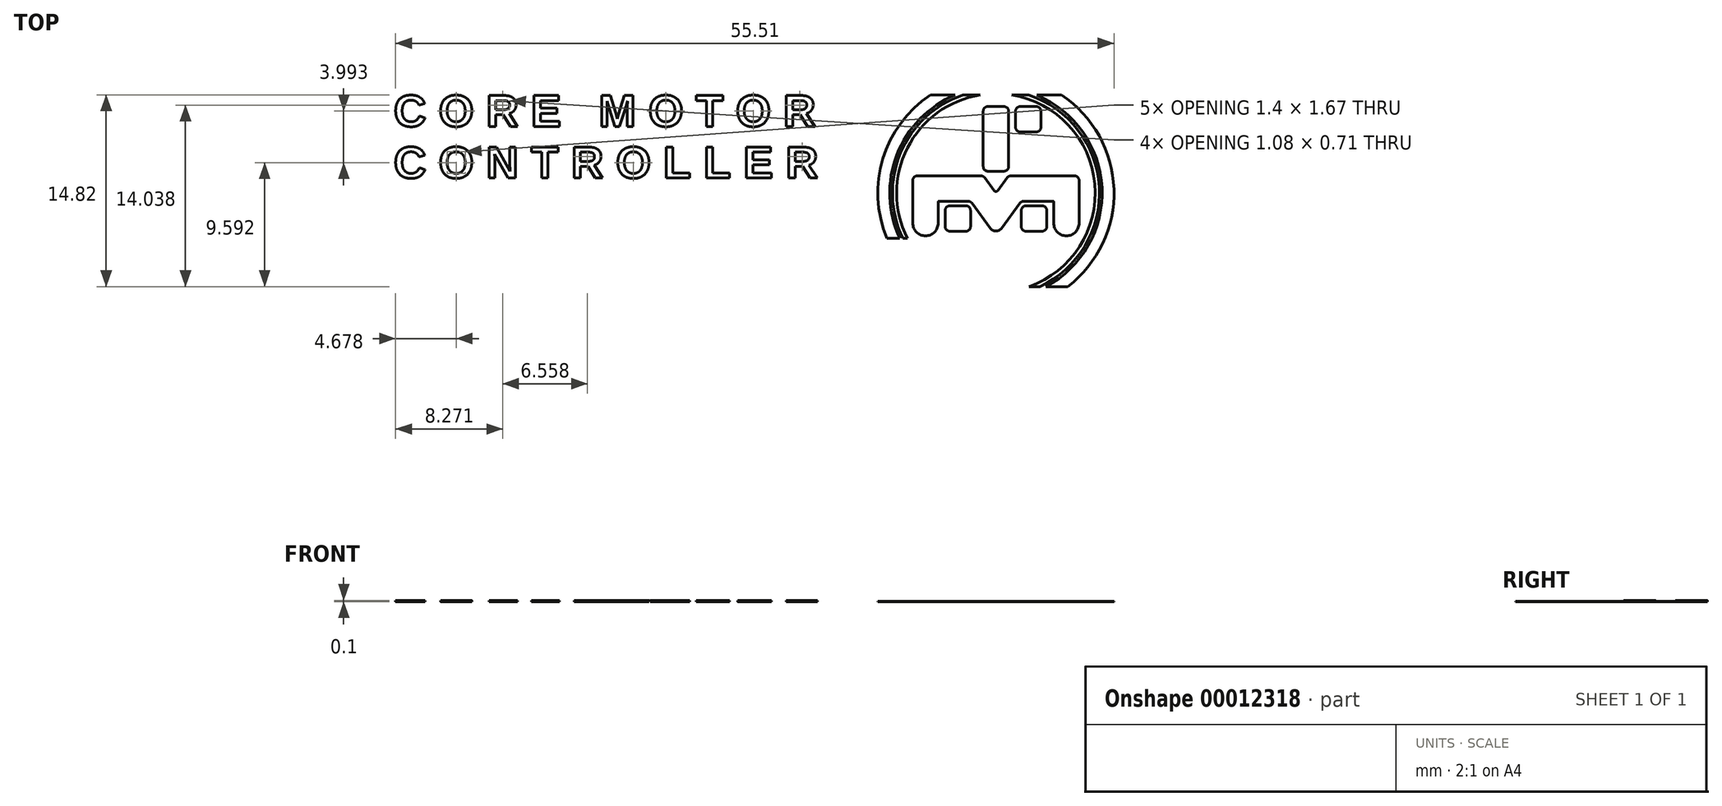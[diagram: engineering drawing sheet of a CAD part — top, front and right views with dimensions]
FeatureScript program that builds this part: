
annotation { "Feature Type Name" : "Feature", "Feature Type Description" : "" }
export const myFeature = defineFeature(function(context is Context, id is Id, definition is map)
    precondition{}
    {
        {
            var Q0;
            Q0=qCreatedBy(makeId("Top.planeOp"),FACE);
            var sketch = newSketch(context, id + "F0", { "sketchPlane" : qUnion([Q0])});
            skLineSegment(sketch, "E0.bottom", {"start": v(62.75, -5.5) * mm, "end": v(66.25, -5.5) * mm});
            skLineSegment(sketch, "E0.top", {"start": v(62.75, -19.5) * mm, "end": v(66.25, -19.5) * mm});
            skLineSegment(sketch, "E0.left", {"start": v(61.75, -6.5) * mm, "end": v(61.75, -18.5) * mm});
            skLineSegment(sketch, "E0.right", {"start": v(67.25, -6.5) * mm, "end": v(67.25, -18.5) * mm});
            skLineSegment(sketch, "E1.bottom", {"start": v(69.75, -5.5) * mm, "end": v(73.25, -5.5) * mm});
            skLineSegment(sketch, "E1.top", {"start": v(69.75, -11) * mm, "end": v(73.25, -11) * mm});
            skLineSegment(sketch, "E1.left", {"start": v(68.75, -6.5) * mm, "end": v(68.75, -10) * mm});
            skLineSegment(sketch, "E1.right", {"start": v(74.25, -6.5) * mm, "end": v(74.25, -10) * mm});
            skLineSegment(sketch, "E2", {"start": v(64.5, -19.5) * mm, "end": v(64.5, -33.5) * mm, "construction": true});
            skLineSegment(sketch, "E3", {"start": v(63.3, -31.86) * mm, "end": v(59.27, -26.4) * mm});
            skLineSegment(sketch, "E4", {"start": v(58.47, -26) * mm, "end": v(52.1, -26) * mm});
            skLineSegment(sketch, "E5", {"start": v(52, -26.1) * mm, "end": v(52, -30.75) * mm});
            skLineSegment(sketch, "E6.0", {"start": v(46.5, -21.5) * mm, "end": v(46.5, -30.75) * mm});
            skLineSegment(sketch, "E6.1", {"start": v(61.24, -20.5) * mm, "end": v(47.5, -20.5) * mm});
            skLineSegment(sketch, "E6.2", {"start": v(64.1, -23.68) * mm, "end": v(62.05, -20.9) * mm});
            skLineSegment(sketch, "E7", {"start": v(49.25, -33.5) * mm, "end": v(49.25, -33.5) * mm});
            skPoint(sketch, "E8.orphan", {"position": v(52, -33.5) * mm});
            skPoint(sketch, "E9.visualSharp", {"position": v(46.5, -33.5) * mm});
            skArc(sketch, "E9.filletArc", {"start": v(46.5, -30.75) * mm, "mid": v(47.3, -32.7) * mm, "end": v(49.25, -33.5) * mm});
            skArc(sketch, "E10.filletArc", {"start": v(49.25, -33.5) * mm, "mid": v(51.2, -32.7) * mm, "end": v(52, -30.75) * mm});
            skLineSegment(sketch, "E11.right", {"start": v(59, -28) * mm, "end": v(59, -31.5) * mm});
            skLineSegment(sketch, "E11.left", {"start": v(53.5, -28) * mm, "end": v(53.5, -31.5) * mm});
            skLineSegment(sketch, "E11.top", {"start": v(54.5, -32.5) * mm, "end": v(58, -32.5) * mm});
            skLineSegment(sketch, "E11.bottom", {"start": v(54.5, -27) * mm, "end": v(58, -27) * mm});
            skPoint(sketch, "E12.0.MirrorP", {"position": v(77, -33.5) * mm});
            skLineSegment(sketch, "E12.1.MirrorCS", {"start": v(74.5, -27) * mm, "end": v(71, -27) * mm});
            skPoint(sketch, "E12.2.MirrorP", {"position": v(82.5, -33.5) * mm});
            skLineSegment(sketch, "E12.3.MirrorCS", {"start": v(70, -28) * mm, "end": v(70, -31.5) * mm});
            skLineSegment(sketch, "E12.4.MirrorCS", {"start": v(75.5, -28) * mm, "end": v(75.5, -31.5) * mm});
            skLineSegment(sketch, "E12.5.MirrorCS", {"start": v(74.5, -32.5) * mm, "end": v(71, -32.5) * mm});
            skLineSegment(sketch, "E12.6.MirrorCS", {"start": v(70.53, -26) * mm, "end": v(76.9, -26) * mm});
            skLineSegment(sketch, "E12.7.MirrorCS", {"start": v(77, -26.1) * mm, "end": v(77, -30.75) * mm});
            skArc(sketch, "E12.8.MirrorCS", {"start": v(79.75, -33.5) * mm, "mid": v(77.8, -32.7) * mm, "end": v(77, -30.75) * mm});
            skLineSegment(sketch, "E12.9.MirrorCS", {"start": v(79.75, -33.5) * mm, "end": v(79.75, -33.5) * mm});
            skLineSegment(sketch, "E12.10.MirrorCS", {"start": v(67.76, -20.5) * mm, "end": v(81.5, -20.5) * mm});
            skPoint(sketch, "E12.11.MirrorP", {"position": v(77, -33.5) * mm});
            skLineSegment(sketch, "E12.12.MirrorCS", {"start": v(64.9, -23.68) * mm, "end": v(66.95, -20.9) * mm});
            skArc(sketch, "E12.13.MirrorCS", {"start": v(82.5, -30.75) * mm, "mid": v(81.7, -32.7) * mm, "end": v(79.75, -33.5) * mm});
            skLineSegment(sketch, "E12.14.MirrorCS", {"start": v(65.7, -31.86) * mm, "end": v(69.73, -26.4) * mm});
            skLineSegment(sketch, "E12.15.MirrorCS", {"start": v(82.5, -21.5) * mm, "end": v(82.5, -30.75) * mm});
            skPoint(sketch, "E13.visualSharp", {"position": v(68.75, -5.5) * mm});
            skArc(sketch, "E13.filletArc", {"start": v(69.75, -5.5) * mm, "mid": v(69.04, -5.8) * mm, "end": v(68.75, -6.5) * mm});
            skPoint(sketch, "E14.visualSharp", {"position": v(74.25, -5.5) * mm});
            skArc(sketch, "E14.filletArc", {"start": v(74.25, -6.5) * mm, "mid": v(73.96, -5.8) * mm, "end": v(73.25, -5.5) * mm});
            skPoint(sketch, "E15.visualSharp", {"position": v(74.25, -11) * mm});
            skArc(sketch, "E15.filletArc", {"start": v(73.25, -11) * mm, "mid": v(73.96, -10.7) * mm, "end": v(74.25, -10) * mm});
            skPoint(sketch, "E16.visualSharp", {"position": v(68.75, -11) * mm});
            skArc(sketch, "E16.filletArc", {"start": v(68.75, -10) * mm, "mid": v(69.04, -10.7) * mm, "end": v(69.75, -11) * mm});
            skPoint(sketch, "E17.visualSharp", {"position": v(67.25, -5.5) * mm});
            skArc(sketch, "E17.filletArc", {"start": v(67.25, -6.5) * mm, "mid": v(66.96, -5.8) * mm, "end": v(66.25, -5.5) * mm});
            skPoint(sketch, "E18.visualSharp", {"position": v(61.75, -5.5) * mm});
            skArc(sketch, "E18.filletArc", {"start": v(62.75, -5.5) * mm, "mid": v(62.04, -5.8) * mm, "end": v(61.75, -6.5) * mm});
            skPoint(sketch, "E19.visualSharp", {"position": v(61.75, -19.5) * mm});
            skArc(sketch, "E19.filletArc", {"start": v(61.75, -18.5) * mm, "mid": v(62.04, -19.2) * mm, "end": v(62.75, -19.5) * mm});
            skPoint(sketch, "E20.visualSharp", {"position": v(67.25, -19.5) * mm});
            skArc(sketch, "E20.filletArc", {"start": v(66.25, -19.5) * mm, "mid": v(66.96, -19.2) * mm, "end": v(67.25, -18.5) * mm});
            skPoint(sketch, "E21.visualSharp", {"position": v(70, -32.5) * mm});
            skArc(sketch, "E21.filletArc", {"start": v(70, -31.5) * mm, "mid": v(70.3, -32.2) * mm, "end": v(71, -32.5) * mm});
            skPoint(sketch, "E22.visualSharp", {"position": v(75.5, -27) * mm});
            skArc(sketch, "E22.filletArc", {"start": v(75.5, -28) * mm, "mid": v(75.2, -27.3) * mm, "end": v(74.5, -27) * mm});
            skPoint(sketch, "E23.visualSharp", {"position": v(70, -27) * mm});
            skArc(sketch, "E23.filletArc", {"start": v(71, -27) * mm, "mid": v(70.3, -27.3) * mm, "end": v(70, -28) * mm});
            skPoint(sketch, "E24.visualSharp", {"position": v(75.5, -32.5) * mm});
            skArc(sketch, "E24.filletArc", {"start": v(74.5, -32.5) * mm, "mid": v(75.2, -32.2) * mm, "end": v(75.5, -31.5) * mm});
            skPoint(sketch, "E25.visualSharp", {"position": v(59, -32.5) * mm});
            skArc(sketch, "E25.filletArc", {"start": v(58, -32.5) * mm, "mid": v(58.7, -32.2) * mm, "end": v(59, -31.5) * mm});
            skPoint(sketch, "E26.visualSharp", {"position": v(59, -27) * mm});
            skArc(sketch, "E26.filletArc", {"start": v(59, -28) * mm, "mid": v(58.7, -27.3) * mm, "end": v(58, -27) * mm});
            skPoint(sketch, "E27.visualSharp", {"position": v(53.5, -27) * mm});
            skArc(sketch, "E27.filletArc", {"start": v(54.5, -27) * mm, "mid": v(53.8, -27.3) * mm, "end": v(53.5, -28) * mm});
            skPoint(sketch, "E28.visualSharp", {"position": v(53.5, -32.5) * mm});
            skArc(sketch, "E28.filletArc", {"start": v(53.5, -31.5) * mm, "mid": v(53.8, -32.2) * mm, "end": v(54.5, -32.5) * mm});
            skPoint(sketch, "E29.visualSharp", {"position": v(46.5, -20.5) * mm});
            skArc(sketch, "E29.filletArc", {"start": v(47.5, -20.5) * mm, "mid": v(46.8, -20.8) * mm, "end": v(46.5, -21.5) * mm});
            skPoint(sketch, "E30.visualSharp", {"position": v(82.5, -20.5) * mm});
            skArc(sketch, "E30.filletArc", {"start": v(82.5, -21.5) * mm, "mid": v(82.2, -20.8) * mm, "end": v(81.5, -20.5) * mm});
            skPoint(sketch, "E31.visualSharp", {"position": v(61.75, -20.5) * mm});
            skArc(sketch, "E31.filletArc", {"start": v(62.05, -20.9) * mm, "mid": v(61.7, -20.6) * mm, "end": v(61.24, -20.5) * mm});
            skPoint(sketch, "E32.visualSharp", {"position": v(67.25, -20.5) * mm});
            skArc(sketch, "E32.filletArc", {"start": v(67.76, -20.5) * mm, "mid": v(67.3, -20.6) * mm, "end": v(66.95, -20.9) * mm});
            skPoint(sketch, "E33.visualSharp", {"position": v(52, -26) * mm});
            skArc(sketch, "E33.filletArc", {"start": v(52.1, -26) * mm, "mid": v(52.03, -26.03) * mm, "end": v(52, -26.1) * mm});
            skPoint(sketch, "E34.visualSharp", {"position": v(77, -26) * mm});
            skArc(sketch, "E34.filletArc", {"start": v(77, -26.1) * mm, "mid": v(76.97, -26.03) * mm, "end": v(76.9, -26) * mm});
            skPoint(sketch, "E35.visualSharp", {"position": v(70.03, -26) * mm});
            skArc(sketch, "E35.filletArc", {"start": v(70.53, -26) * mm, "mid": v(70.08, -26.1) * mm, "end": v(69.73, -26.4) * mm});
            skPoint(sketch, "E36.visualSharp", {"position": v(58.97, -26) * mm});
            skArc(sketch, "E36.filletArc", {"start": v(59.27, -26.4) * mm, "mid": v(58.92, -26.1) * mm, "end": v(58.47, -26) * mm});
            skPoint(sketch, "E37.visualSharp", {"position": v(64.5, -33.5) * mm});
            skArc(sketch, "E37.filletArc", {"start": v(63.3, -31.86) * mm, "mid": v(64.5, -32.47) * mm, "end": v(65.7, -31.86) * mm});
            skPoint(sketch, "E38.visualSharp", {"position": v(64.5, -24.23) * mm});
            skArc(sketch, "E38.filletArc", {"start": v(64.1, -23.68) * mm, "mid": v(64.5, -23.89) * mm, "end": v(64.9, -23.68) * mm});
            skArc(sketch, "E39", {"start": v(71.68, -44.5) * mm, "mid": v(85.92, -22.29) * mm, "end": v(67.92, -3) * mm});
            skArc(sketch, "E40", {"start": v(74, -44.5) * mm, "mid": v(86.85, -22.94) * mm, "end": v(71.6, -3) * mm});
            skArc(sketch, "E41", {"start": v(75.35, -44.5) * mm, "mid": v(87.46, -23.1) * mm, "end": v(73.32, -3) * mm});
            skArc(sketch, "E42", {"start": v(80.06, -44.5) * mm, "mid": v(90.04, -23.4) * mm, "end": v(78.72, -3) * mm});
            skLineSegment(sketch, "E43", {"start": v(80.06, -44.5) * mm, "end": v(75.35, -44.5) * mm});
            skLineSegment(sketch, "E44.trimOffspring", {"start": v(74, -44.5) * mm, "end": v(71.68, -44.5) * mm});
            skLineSegment(sketch, "E45", {"start": v(40.9, -34) * mm, "end": v(43.69, -34) * mm});
            skLineSegment(sketch, "E46.trimOffspring", {"start": v(44.36, -34) * mm, "end": v(45.34, -34) * mm});
            skLineSegment(sketch, "E47", {"start": v(50.28, -3) * mm, "end": v(55.68, -3) * mm});
            skArc(sketch, "E48.trimOffspring", {"start": v(61.08, -3) * mm, "mid": v(45.33, -14.5) * mm, "end": v(45.34, -34) * mm});
            skArc(sketch, "E49.trimOffspring", {"start": v(50.28, -3) * mm, "mid": v(40.05, -16.82) * mm, "end": v(40.9, -34) * mm});
            skArc(sketch, "E50.trimOffspring", {"start": v(55.68, -3) * mm, "mid": v(43.06, -15.94) * mm, "end": v(43.69, -34) * mm});
            skArc(sketch, "E51.trimOffspring", {"start": v(57.4, -3) * mm, "mid": v(43.86, -15.55) * mm, "end": v(44.36, -34) * mm});
            skLineSegment(sketch, "E52.trimOffspring", {"start": v(67.92, -3) * mm, "end": v(71.6, -3) * mm});
            skLineSegment(sketch, "E53.trimOffspring", {"start": v(57.4, -3) * mm, "end": v(61.08, -3) * mm});
            skLineSegment(sketch, "E54.trimOffspring", {"start": v(73.32, -3) * mm, "end": v(78.72, -3) * mm});
            skSolve(sketch);
        }
        {
            var Q0;
            Q0=makeQuery(id+"F0.imprint","IMPRINT",FACE,{"disambiguationData":[TD([[makeQuery(id+"F0.imprint","IMPRINT",EDGE,{"derivedFrom":sQuery(id+"F0.wireOp",EDGE,"46c11c21-c6ca-42b8-9659-15b4f280ee3c.sketch_text.stroke-197")}),1.0]])]});
            var Q1;
            Q1=makeQuery(id+"F0.imprint","IMPRINT",FACE,{"disambiguationData":[TD([[makeQuery(id+"F0.imprint","IMPRINT",EDGE,{"derivedFrom":sQuery(id+"F0.wireOp",EDGE,"E1.bottom")}),-1.0]])]});
            var Q2;
            Q2=makeQuery(id+"F0.imprint","IMPRINT",FACE,{"disambiguationData":[TD([[makeQuery(id+"F0.imprint","IMPRINT",EDGE,{"derivedFrom":sQuery(id+"F0.wireOp",EDGE,"46c11c21-c6ca-42b8-9659-15b4f280ee3c.sketch_text.stroke-126")}),-1.0]])]});
            var Q3;
            Q3=makeQuery(id+"F0.imprint","IMPRINT",FACE,{"disambiguationData":[TD([[makeQuery(id+"F0.imprint","IMPRINT",EDGE,{"derivedFrom":sQuery(id+"F0.wireOp",EDGE,"46c11c21-c6ca-42b8-9659-15b4f280ee3c.sketch_text.stroke-360")}),-1.0]])]});
            var Q4;
            Q4=makeQuery(id+"F0.imprint","IMPRINT",FACE,{"disambiguationData":[TD([[makeQuery(id+"F0.imprint","IMPRINT",EDGE,{"derivedFrom":sQuery(id+"F0.wireOp",EDGE,"E0.bottom")}),-1.0]])]});
            var Q5;
            Q5=makeQuery(id+"F0.imprint","IMPRINT",FACE,{"disambiguationData":[TD([[makeQuery(id+"F0.imprint","IMPRINT",EDGE,{"derivedFrom":sQuery(id+"F0.wireOp",EDGE,"46c11c21-c6ca-42b8-9659-15b4f280ee3c.sketch_text.stroke-0")}),-1.0]])]});
            var Q6;
            Q6=makeQuery(id+"F0.imprint","IMPRINT",FACE,{"disambiguationData":[TD([[makeQuery(id+"F0.imprint","IMPRINT",EDGE,{"derivedFrom":sQuery(id+"F0.wireOp",EDGE,"46c11c21-c6ca-42b8-9659-15b4f280ee3c.sketch_text.stroke-90")}),-1.0]])]});
            var Q7;
            Q7=makeQuery(id+"F0.imprint","IMPRINT",FACE,{"disambiguationData":[TD([[makeQuery(id+"F0.imprint","IMPRINT",EDGE,{"derivedFrom":sQuery(id+"F0.wireOp",EDGE,"46c11c21-c6ca-42b8-9659-15b4f280ee3c.sketch_text.stroke-145")}),-1.0]])]});
            var Q8;
            Q8=makeQuery(id+"F0.imprint","IMPRINT",FACE,{"disambiguationData":[TD([[makeQuery(id+"F0.imprint","IMPRINT",EDGE,{"derivedFrom":sQuery(id+"F0.wireOp",EDGE,"46c11c21-c6ca-42b8-9659-15b4f280ee3c.sketch_text.stroke-126")}),1.0]])]});
            var Q9;
            Q9=makeQuery(id+"F0.imprint","IMPRINT",FACE,{"disambiguationData":[TD([[makeQuery(id+"F0.imprint","IMPRINT",EDGE,{"derivedFrom":sQuery(id+"F0.wireOp",EDGE,"46c11c21-c6ca-42b8-9659-15b4f280ee3c.sketch_text.stroke-48")}),-1.0]])]});
            var Q10;
            Q10=makeQuery(id+"F0.imprint","IMPRINT",FACE,{"disambiguationData":[TD([[makeQuery(id+"F0.imprint","IMPRINT",EDGE,{"derivedFrom":sQuery(id+"F0.wireOp",EDGE,"46c11c21-c6ca-42b8-9659-15b4f280ee3c.sketch_text.stroke-239")}),1.0]])]});
            var Q11;
            Q11=makeQuery(id+"F0.imprint","IMPRINT",FACE,{"disambiguationData":[TD([[makeQuery(id+"F0.imprint","IMPRINT",EDGE,{"derivedFrom":sQuery(id+"F0.wireOp",EDGE,"E12.1.MirrorCS")}),1.0]])]});
            var Q12;
            Q12=makeQuery(id+"F0.imprint","IMPRINT",FACE,{"disambiguationData":[TD([[makeQuery(id+"F0.imprint","IMPRINT",EDGE,{"derivedFrom":sQuery(id+"F0.wireOp",EDGE,"46c11c21-c6ca-42b8-9659-15b4f280ee3c.sketch_text.stroke-300")}),-1.0]])]});
            var Q13;
            Q13=makeQuery(id+"F0.imprint","IMPRINT",FACE,{"disambiguationData":[TD([[makeQuery(id+"F0.imprint","IMPRINT",EDGE,{"derivedFrom":sQuery(id+"F0.wireOp",EDGE,"46c11c21-c6ca-42b8-9659-15b4f280ee3c.sketch_text.stroke-245")}),-1.0]])]});
            var Q14;
            Q14=makeQuery(id+"F0.imprint","IMPRINT",FACE,{"disambiguationData":[TD([[makeQuery(id+"F0.imprint","IMPRINT",EDGE,{"derivedFrom":sQuery(id+"F0.wireOp",EDGE,"46c11c21-c6ca-42b8-9659-15b4f280ee3c.sketch_text.stroke-268")}),-1.0]])]});
            var Q15;
            Q15=makeQuery(id+"F0.imprint","IMPRINT",FACE,{"disambiguationData":[TD([[makeQuery(id+"F0.imprint","IMPRINT",EDGE,{"derivedFrom":sQuery(id+"F0.wireOp",EDGE,"46c11c21-c6ca-42b8-9659-15b4f280ee3c.sketch_text.stroke-189")}),-1.0]])]});
            var Q16;
            Q16=makeQuery(id+"F0.imprint","IMPRINT",FACE,{"disambiguationData":[TD([[makeQuery(id+"F0.imprint","IMPRINT",EDGE,{"derivedFrom":sQuery(id+"F0.wireOp",EDGE,"46c11c21-c6ca-42b8-9659-15b4f280ee3c.sketch_text.stroke-114")}),-1.0]])]});
            var Q17;
            Q17=makeQuery(id+"F0.imprint","IMPRINT",FACE,{"disambiguationData":[TD([[makeQuery(id+"F0.imprint","IMPRINT",EDGE,{"derivedFrom":sQuery(id+"F0.wireOp",EDGE,"E3")}),-1.0]])]});
            var Q18;
            Q18=makeQuery(id+"F0.imprint","IMPRINT",FACE,{"disambiguationData":[TD([[makeQuery(id+"F0.imprint","IMPRINT",EDGE,{"derivedFrom":sQuery(id+"F0.wireOp",EDGE,"46c11c21-c6ca-42b8-9659-15b4f280ee3c.sketch_text.stroke-345")}),-1.0]])]});
            var Q19;
            Q19=makeQuery(id+"F0.imprint","IMPRINT",FACE,{"disambiguationData":[TD([[makeQuery(id+"F0.imprint","IMPRINT",EDGE,{"derivedFrom":sQuery(id+"F0.wireOp",EDGE,"46c11c21-c6ca-42b8-9659-15b4f280ee3c.sketch_text.stroke-232")}),1.0]])]});
            var Q20;
            Q20=makeQuery(id+"F0.imprint","IMPRINT",FACE,{"disambiguationData":[TD([[makeQuery(id+"F0.imprint","IMPRINT",EDGE,{"derivedFrom":sQuery(id+"F0.wireOp",EDGE,"46c11c21-c6ca-42b8-9659-15b4f280ee3c.sketch_text.stroke-280")}),1.0]])]});
            var Q21;
            Q21=makeQuery(id+"F0.imprint","IMPRINT",FACE,{"disambiguationData":[TD([[makeQuery(id+"F0.imprint","IMPRINT",EDGE,{"derivedFrom":sQuery(id+"F0.wireOp",EDGE,"46c11c21-c6ca-42b8-9659-15b4f280ee3c.sketch_text.stroke-161")}),-1.0]])]});
            var Q22;
            Q22=makeQuery(id+"F0.imprint","IMPRINT",FACE,{"disambiguationData":[TD([[makeQuery(id+"F0.imprint","IMPRINT",EDGE,{"derivedFrom":sQuery(id+"F0.wireOp",EDGE,"46c11c21-c6ca-42b8-9659-15b4f280ee3c.sketch_text.stroke-157")}),-1.0]])]});
            var Q23;
            Q23=makeQuery(id+"F0.imprint","IMPRINT",FACE,{"disambiguationData":[TD([[makeQuery(id+"F0.imprint","IMPRINT",EDGE,{"derivedFrom":sQuery(id+"F0.wireOp",EDGE,"46c11c21-c6ca-42b8-9659-15b4f280ee3c.sketch_text.stroke-84")}),1.0]])]});
            var Q24;
            Q24=makeQuery(id+"F0.imprint","IMPRINT",FACE,{"disambiguationData":[TD([[makeQuery(id+"F0.imprint","IMPRINT",EDGE,{"derivedFrom":sQuery(id+"F0.wireOp",EDGE,"46c11c21-c6ca-42b8-9659-15b4f280ee3c.sketch_text.stroke-60")}),-1.0]])]});
            var Q25;
            Q25=makeQuery(id+"F0.imprint","IMPRINT",FACE,{"disambiguationData":[TD([[makeQuery(id+"F0.imprint","IMPRINT",EDGE,{"derivedFrom":sQuery(id+"F0.wireOp",EDGE,"46c11c21-c6ca-42b8-9659-15b4f280ee3c.sketch_text.stroke-340")}),1.0]])]});
            var Q26;
            Q26=makeQuery(id+"F0.imprint","IMPRINT",FACE,{"disambiguationData":[TD([[makeQuery(id+"F0.imprint","IMPRINT",EDGE,{"derivedFrom":sQuery(id+"F0.wireOp",EDGE,"46c11c21-c6ca-42b8-9659-15b4f280ee3c.sketch_text.stroke-220")}),-1.0]])]});
            var Q27;
            Q27=makeQuery(id+"F0.imprint","IMPRINT",FACE,{"disambiguationData":[TD([[makeQuery(id+"F0.imprint","IMPRINT",EDGE,{"derivedFrom":sQuery(id+"F0.wireOp",EDGE,"46c11c21-c6ca-42b8-9659-15b4f280ee3c.sketch_text.stroke-76")}),-1.0]])]});
            var Q28;
            Q28=makeQuery(id+"F0.imprint","IMPRINT",FACE,{"disambiguationData":[TD([[makeQuery(id+"F0.imprint","IMPRINT",EDGE,{"derivedFrom":sQuery(id+"F0.wireOp",EDGE,"46c11c21-c6ca-42b8-9659-15b4f280ee3c.sketch_text.stroke-327")}),1.0]])]});
            var Q29;
            Q29=makeQuery(id+"F0.imprint","IMPRINT",FACE,{"disambiguationData":[TD([[makeQuery(id+"F0.imprint","IMPRINT",EDGE,{"derivedFrom":sQuery(id+"F0.wireOp",EDGE,"46c11c21-c6ca-42b8-9659-15b4f280ee3c.sketch_text.stroke-29")}),-1.0]])]});
            var Q30;
            Q30=makeQuery(id+"F0.imprint","IMPRINT",FACE,{"disambiguationData":[TD([[makeQuery(id+"F0.imprint","IMPRINT",EDGE,{"derivedFrom":sQuery(id+"F0.wireOp",EDGE,"46c11c21-c6ca-42b8-9659-15b4f280ee3c.sketch_text.stroke-60")}),1.0]])]});
            var Q31;
            Q31=makeQuery(id+"F0.imprint","IMPRINT",FACE,{"disambiguationData":[TD([[makeQuery(id+"F0.imprint","IMPRINT",EDGE,{"derivedFrom":sQuery(id+"F0.wireOp",EDGE,"46c11c21-c6ca-42b8-9659-15b4f280ee3c.sketch_text.stroke-333")}),-1.0]])]});
            var Q32;
            Q32=makeQuery(id+"F0.imprint","IMPRINT",FACE,{"disambiguationData":[TD([[makeQuery(id+"F0.imprint","IMPRINT",EDGE,{"derivedFrom":sQuery(id+"F0.wireOp",EDGE,"E11.right")}),-1.0]])]});
            var Q33;
            Q33=makeQuery(id+"F0.imprint","IMPRINT",FACE,{"disambiguationData":[TD([[makeQuery(id+"F0.imprint","IMPRINT",EDGE,{"derivedFrom":sQuery(id+"F0.wireOp",EDGE,"46c11c21-c6ca-42b8-9659-15b4f280ee3c.sketch_text.stroke-216")}),-1.0]])]});
            var Q34;
            Q34=makeQuery(id+"F0.imprint","IMPRINT",FACE,{"disambiguationData":[TD([[makeQuery(id+"F0.imprint","IMPRINT",EDGE,{"derivedFrom":sQuery(id+"F0.wireOp",EDGE,"46c11c21-c6ca-42b8-9659-15b4f280ee3c.sketch_text.stroke-260")}),-1.0]])]});
            var Q35;
            Q35=makeQuery(id+"F0.imprint","IMPRINT",FACE,{"disambiguationData":[TD([[makeQuery(id+"F0.imprint","IMPRINT",EDGE,{"derivedFrom":sQuery(id+"F0.wireOp",EDGE,"46c11c21-c6ca-42b8-9659-15b4f280ee3c.sketch_text.stroke-286")}),-1.0]])]});
            var Q36;
            Q36=makeQuery(id+"F0.imprint","IMPRINT",FACE,{"disambiguationData":[TD([[makeQuery(id+"F0.imprint","IMPRINT",EDGE,{"derivedFrom":sQuery(id+"F0.wireOp",EDGE,"46c11c21-c6ca-42b8-9659-15b4f280ee3c.sketch_text.stroke-197")}),-1.0]])]});
            var Q37;
            Q37=makeQuery(id+"F0.imprint","IMPRINT",FACE,{"disambiguationData":[TD([[makeQuery(id+"F0.imprint","IMPRINT",EDGE,{"derivedFrom":sQuery(id+"F0.wireOp",EDGE,"46c11c21-c6ca-42b8-9659-15b4f280ee3c.sketch_text.stroke-319")}),-1.0]])]});
            var Q38;
            Q38=makeQuery(id+"F0.imprint","IMPRINT",FACE,{"disambiguationData":[TD([[makeQuery(id+"F0.imprint","IMPRINT",EDGE,{"derivedFrom":sQuery(id+"F0.wireOp",EDGE,"46c11c21-c6ca-42b8-9659-15b4f280ee3c.sketch_text.stroke-366")}),-1.0]])]});
            var Q39;
            Q39=makeQuery(id+"F0.imprint","IMPRINT",FACE,{"disambiguationData":[TD([[makeQuery(id+"F0.imprint","IMPRINT",EDGE,{"derivedFrom":sQuery(id+"F0.wireOp",EDGE,"46c11c21-c6ca-42b8-9659-15b4f280ee3c.sketch_text.stroke-272")}),-1.0]])]});
            var Q40;
            Q40=makeQuery(id+"F0.imprint","IMPRINT",FACE,{"disambiguationData":[TD([[makeQuery(id+"F0.imprint","IMPRINT",EDGE,{"derivedFrom":sQuery(id+"F0.wireOp",EDGE,"46c11c21-c6ca-42b8-9659-15b4f280ee3c.sketch_text.stroke-15")}),-1.0]])]});
            var Q41;
            Q41=makeQuery(id+"F0.imprint","IMPRINT",FACE,{"disambiguationData":[TD([[makeQuery(id+"F0.imprint","IMPRINT",EDGE,{"derivedFrom":sQuery(id+"F0.wireOp",EDGE,"46c11c21-c6ca-42b8-9659-15b4f280ee3c.sketch_text.stroke-168")}),-1.0]])]});
            var Q42;
            Q42=makeQuery(id+"F0.imprint","IMPRINT",FACE,{"disambiguationData":[TD([[makeQuery(id+"F0.imprint","IMPRINT",EDGE,{"derivedFrom":sQuery(id+"F0.wireOp",EDGE,"46c11c21-c6ca-42b8-9659-15b4f280ee3c.sketch_text.stroke-95")}),-1.0]])]});
            var Q43;
            Q43=makeQuery(id+"F0.imprint","IMPRINT",FACE,{"disambiguationData":[TD([[makeQuery(id+"F0.imprint","IMPRINT",EDGE,{"derivedFrom":sQuery(id+"F0.wireOp",EDGE,"46c11c21-c6ca-42b8-9659-15b4f280ee3c.sketch_text.stroke-225")}),-1.0]])]});
            var Q44;
            Q44=makeQuery(id+"F0.imprint","IMPRINT",FACE,{"disambiguationData":[TD([[makeQuery(id+"F0.imprint","IMPRINT",EDGE,{"derivedFrom":sQuery(id+"F0.wireOp",EDGE,"46c11c21-c6ca-42b8-9659-15b4f280ee3c.sketch_text.stroke-231")}),-1.0]])]});
            var Q45;
            Q45=makeQuery(id+"F0.imprint","IMPRINT",FACE,{"disambiguationData":[TD([[makeQuery(id+"F0.imprint","IMPRINT",EDGE,{"derivedFrom":sQuery(id+"F0.wireOp",EDGE,"46c11c21-c6ca-42b8-9659-15b4f280ee3c.sketch_text.stroke-177")}),-1.0]])]});
            var Q46;
            Q46=makeQuery(id+"F0.imprint","IMPRINT",FACE,{"disambiguationData":[TD([[makeQuery(id+"F0.imprint","IMPRINT",EDGE,{"derivedFrom":sQuery(id+"F0.wireOp",EDGE,"E41")}),-1.0]])]});
            var Q47;
            Q47=makeQuery(id+"F0.imprint","IMPRINT",FACE,{"disambiguationData":[TD([[makeQuery(id+"F0.imprint","IMPRINT",EDGE,{"derivedFrom":sQuery(id+"F0.wireOp",EDGE,"E39")}),-1.0]])]});
            var Q48;
            Q48=makeQuery(id+"F0.imprint","IMPRINT",FACE,{"disambiguationData":[TD([[makeQuery(id+"F0.imprint","IMPRINT",EDGE,{"derivedFrom":sQuery(id+"F0.wireOp",EDGE,"E45")}),1.0]])]});
            var Q49;
            Q49=makeQuery(id+"F0.imprint","IMPRINT",FACE,{"disambiguationData":[TD([[makeQuery(id+"F0.imprint","IMPRINT",EDGE,{"derivedFrom":sQuery(id+"F0.wireOp",EDGE,"E46.trimOffspring")}),1.0]])]});
            extrude(context, id + "F1", {"entities" : qUnion([Q0, Q1, Q2, Q3, Q4, Q5, Q6, Q7, Q8, Q9, Q10, Q11, Q12, Q13, Q14, Q15, Q16, Q17, Q18, Q19, Q20, Q21, Q22, Q23, Q24, Q25, Q26, Q27, Q28, Q29, Q30, Q31, Q32, Q33, Q34, Q35, Q36, Q37, Q38, Q39, Q40, Q41, Q42, Q43, Q44, Q45, Q46, Q47, Q48, Q49]), "depth" : .1 * mm});
        }
        {
            var Q0;
            Q0=makeQuery(id+"F1.opExtrude","SWEPT_BODY",BODY,{"disambiguationData":[OSD([sQuery(id+"F0.wireOp",EDGE,"46c11c21-c6ca-42b8-9659-15b4f280ee3c.sketch_text.stroke-149"),sQuery(id+"F0.wireOp",EDGE,"46c11c21-c6ca-42b8-9659-15b4f280ee3c.sketch_text.stroke-150"),sQuery(id+"F0.wireOp",EDGE,"46c11c21-c6ca-42b8-9659-15b4f280ee3c.sketch_text.stroke-151"),sQuery(id+"F0.wireOp",EDGE,"46c11c21-c6ca-42b8-9659-15b4f280ee3c.sketch_text.stroke-152"),sQuery(id+"F0.wireOp",EDGE,"46c11c21-c6ca-42b8-9659-15b4f280ee3c.sketch_text.stroke-153"),sQuery(id+"F0.wireOp",EDGE,"46c11c21-c6ca-42b8-9659-15b4f280ee3c.sketch_text.stroke-154"),sQuery(id+"F0.wireOp",EDGE,"46c11c21-c6ca-42b8-9659-15b4f280ee3c.sketch_text.stroke-155"),sQuery(id+"F0.wireOp",EDGE,"46c11c21-c6ca-42b8-9659-15b4f280ee3c.sketch_text.stroke-156"),sQuery(id+"F0.wireOp",EDGE,"46c11c21-c6ca-42b8-9659-15b4f280ee3c.sketch_text.stroke-157"),sQuery(id+"F0.wireOp",EDGE,"46c11c21-c6ca-42b8-9659-15b4f280ee3c.sketch_text.stroke-158"),sQuery(id+"F0.wireOp",EDGE,"46c11c21-c6ca-42b8-9659-15b4f280ee3c.sketch_text.stroke-159"),sQuery(id+"F0.wireOp",EDGE,"46c11c21-c6ca-42b8-9659-15b4f280ee3c.sketch_text.stroke-160"),sQuery(id+"F0.wireOp",EDGE,"46c11c21-c6ca-42b8-9659-15b4f280ee3c.sketch_text.stroke-161"),sQuery(id+"F0.wireOp",EDGE,"46c11c21-c6ca-42b8-9659-15b4f280ee3c.sketch_text.stroke-162")])]});
            var Q1;
            Q1=makeQuery(id+"F1.opExtrude","SWEPT_BODY",BODY,{"disambiguationData":[OSD([sQuery(id+"F0.wireOp",EDGE,"46c11c21-c6ca-42b8-9659-15b4f280ee3c.sketch_text.stroke-134"),sQuery(id+"F0.wireOp",EDGE,"46c11c21-c6ca-42b8-9659-15b4f280ee3c.sketch_text.stroke-135"),sQuery(id+"F0.wireOp",EDGE,"46c11c21-c6ca-42b8-9659-15b4f280ee3c.sketch_text.stroke-136"),sQuery(id+"F0.wireOp",EDGE,"46c11c21-c6ca-42b8-9659-15b4f280ee3c.sketch_text.stroke-137"),sQuery(id+"F0.wireOp",EDGE,"46c11c21-c6ca-42b8-9659-15b4f280ee3c.sketch_text.stroke-138"),sQuery(id+"F0.wireOp",EDGE,"46c11c21-c6ca-42b8-9659-15b4f280ee3c.sketch_text.stroke-139"),sQuery(id+"F0.wireOp",EDGE,"46c11c21-c6ca-42b8-9659-15b4f280ee3c.sketch_text.stroke-140"),sQuery(id+"F0.wireOp",EDGE,"46c11c21-c6ca-42b8-9659-15b4f280ee3c.sketch_text.stroke-141"),sQuery(id+"F0.wireOp",EDGE,"46c11c21-c6ca-42b8-9659-15b4f280ee3c.sketch_text.stroke-142"),sQuery(id+"F0.wireOp",EDGE,"46c11c21-c6ca-42b8-9659-15b4f280ee3c.sketch_text.stroke-143"),sQuery(id+"F0.wireOp",EDGE,"46c11c21-c6ca-42b8-9659-15b4f280ee3c.sketch_text.stroke-144"),sQuery(id+"F0.wireOp",EDGE,"46c11c21-c6ca-42b8-9659-15b4f280ee3c.sketch_text.stroke-145"),sQuery(id+"F0.wireOp",EDGE,"46c11c21-c6ca-42b8-9659-15b4f280ee3c.sketch_text.stroke-146"),sQuery(id+"F0.wireOp",EDGE,"46c11c21-c6ca-42b8-9659-15b4f280ee3c.sketch_text.stroke-147"),sQuery(id+"F0.wireOp",EDGE,"46c11c21-c6ca-42b8-9659-15b4f280ee3c.sketch_text.stroke-148")])]});
            var Q2;
            Q2=makeQuery(id+"F1.opExtrude","SWEPT_BODY",BODY,{"disambiguationData":[OSD([sQuery(id+"F0.wireOp",EDGE,"46c11c21-c6ca-42b8-9659-15b4f280ee3c.sketch_text.stroke-101"),sQuery(id+"F0.wireOp",EDGE,"46c11c21-c6ca-42b8-9659-15b4f280ee3c.sketch_text.stroke-102"),sQuery(id+"F0.wireOp",EDGE,"46c11c21-c6ca-42b8-9659-15b4f280ee3c.sketch_text.stroke-103"),sQuery(id+"F0.wireOp",EDGE,"46c11c21-c6ca-42b8-9659-15b4f280ee3c.sketch_text.stroke-104"),sQuery(id+"F0.wireOp",EDGE,"46c11c21-c6ca-42b8-9659-15b4f280ee3c.sketch_text.stroke-105"),sQuery(id+"F0.wireOp",EDGE,"46c11c21-c6ca-42b8-9659-15b4f280ee3c.sketch_text.stroke-106"),sQuery(id+"F0.wireOp",EDGE,"46c11c21-c6ca-42b8-9659-15b4f280ee3c.sketch_text.stroke-107"),sQuery(id+"F0.wireOp",EDGE,"46c11c21-c6ca-42b8-9659-15b4f280ee3c.sketch_text.stroke-108"),sQuery(id+"F0.wireOp",EDGE,"46c11c21-c6ca-42b8-9659-15b4f280ee3c.sketch_text.stroke-109"),sQuery(id+"F0.wireOp",EDGE,"46c11c21-c6ca-42b8-9659-15b4f280ee3c.sketch_text.stroke-110"),sQuery(id+"F0.wireOp",EDGE,"46c11c21-c6ca-42b8-9659-15b4f280ee3c.sketch_text.stroke-111"),sQuery(id+"F0.wireOp",EDGE,"46c11c21-c6ca-42b8-9659-15b4f280ee3c.sketch_text.stroke-112"),sQuery(id+"F0.wireOp",EDGE,"46c11c21-c6ca-42b8-9659-15b4f280ee3c.sketch_text.stroke-113"),sQuery(id+"F0.wireOp",EDGE,"46c11c21-c6ca-42b8-9659-15b4f280ee3c.sketch_text.stroke-114")])]});
            var Q3;
            Q3=makeQuery(id+"F1.opExtrude","SWEPT_BODY",BODY,{"disambiguationData":[OSD([sQuery(id+"F0.wireOp",EDGE,"46c11c21-c6ca-42b8-9659-15b4f280ee3c.sketch_text.stroke-79"),sQuery(id+"F0.wireOp",EDGE,"46c11c21-c6ca-42b8-9659-15b4f280ee3c.sketch_text.stroke-80"),sQuery(id+"F0.wireOp",EDGE,"46c11c21-c6ca-42b8-9659-15b4f280ee3c.sketch_text.stroke-81"),sQuery(id+"F0.wireOp",EDGE,"46c11c21-c6ca-42b8-9659-15b4f280ee3c.sketch_text.stroke-82"),sQuery(id+"F0.wireOp",EDGE,"46c11c21-c6ca-42b8-9659-15b4f280ee3c.sketch_text.stroke-83"),sQuery(id+"F0.wireOp",EDGE,"46c11c21-c6ca-42b8-9659-15b4f280ee3c.sketch_text.stroke-84"),sQuery(id+"F0.wireOp",EDGE,"46c11c21-c6ca-42b8-9659-15b4f280ee3c.sketch_text.stroke-85"),sQuery(id+"F0.wireOp",EDGE,"46c11c21-c6ca-42b8-9659-15b4f280ee3c.sketch_text.stroke-86"),sQuery(id+"F0.wireOp",EDGE,"46c11c21-c6ca-42b8-9659-15b4f280ee3c.sketch_text.stroke-87"),sQuery(id+"F0.wireOp",EDGE,"46c11c21-c6ca-42b8-9659-15b4f280ee3c.sketch_text.stroke-88"),sQuery(id+"F0.wireOp",EDGE,"46c11c21-c6ca-42b8-9659-15b4f280ee3c.sketch_text.stroke-89"),sQuery(id+"F0.wireOp",EDGE,"46c11c21-c6ca-42b8-9659-15b4f280ee3c.sketch_text.stroke-90"),sQuery(id+"F0.wireOp",EDGE,"46c11c21-c6ca-42b8-9659-15b4f280ee3c.sketch_text.stroke-91"),sQuery(id+"F0.wireOp",EDGE,"46c11c21-c6ca-42b8-9659-15b4f280ee3c.sketch_text.stroke-92")])]});
            var Q4;
            Q4=makeQuery(id+"F1.opExtrude","SWEPT_BODY",BODY,{"disambiguationData":[OSD([sQuery(id+"F0.wireOp",EDGE,"E0.bottom"),sQuery(id+"F0.wireOp",EDGE,"E0.top"),sQuery(id+"F0.wireOp",EDGE,"E0.left"),sQuery(id+"F0.wireOp",EDGE,"E0.right"),sQuery(id+"F0.wireOp",EDGE,"E17.filletArc"),sQuery(id+"F0.wireOp",EDGE,"E18.filletArc"),sQuery(id+"F0.wireOp",EDGE,"E19.filletArc"),sQuery(id+"F0.wireOp",EDGE,"E20.filletArc")])]});
            var Q5;
            Q5=makeQuery(id+"F1.opExtrude","SWEPT_BODY",BODY,{"disambiguationData":[OSD([sQuery(id+"F0.wireOp",EDGE,"46c11c21-c6ca-42b8-9659-15b4f280ee3c.sketch_text.stroke-242"),sQuery(id+"F0.wireOp",EDGE,"46c11c21-c6ca-42b8-9659-15b4f280ee3c.sketch_text.stroke-243"),sQuery(id+"F0.wireOp",EDGE,"46c11c21-c6ca-42b8-9659-15b4f280ee3c.sketch_text.stroke-244"),sQuery(id+"F0.wireOp",EDGE,"46c11c21-c6ca-42b8-9659-15b4f280ee3c.sketch_text.stroke-245"),sQuery(id+"F0.wireOp",EDGE,"46c11c21-c6ca-42b8-9659-15b4f280ee3c.sketch_text.stroke-246"),sQuery(id+"F0.wireOp",EDGE,"46c11c21-c6ca-42b8-9659-15b4f280ee3c.sketch_text.stroke-247"),sQuery(id+"F0.wireOp",EDGE,"46c11c21-c6ca-42b8-9659-15b4f280ee3c.sketch_text.stroke-248"),sQuery(id+"F0.wireOp",EDGE,"46c11c21-c6ca-42b8-9659-15b4f280ee3c.sketch_text.stroke-249"),sQuery(id+"F0.wireOp",EDGE,"46c11c21-c6ca-42b8-9659-15b4f280ee3c.sketch_text.stroke-250"),sQuery(id+"F0.wireOp",EDGE,"46c11c21-c6ca-42b8-9659-15b4f280ee3c.sketch_text.stroke-251"),sQuery(id+"F0.wireOp",EDGE,"46c11c21-c6ca-42b8-9659-15b4f280ee3c.sketch_text.stroke-252"),sQuery(id+"F0.wireOp",EDGE,"46c11c21-c6ca-42b8-9659-15b4f280ee3c.sketch_text.stroke-253"),sQuery(id+"F0.wireOp",EDGE,"46c11c21-c6ca-42b8-9659-15b4f280ee3c.sketch_text.stroke-254"),sQuery(id+"F0.wireOp",EDGE,"46c11c21-c6ca-42b8-9659-15b4f280ee3c.sketch_text.stroke-255"),sQuery(id+"F0.wireOp",EDGE,"46c11c21-c6ca-42b8-9659-15b4f280ee3c.sketch_text.stroke-256"),sQuery(id+"F0.wireOp",EDGE,"46c11c21-c6ca-42b8-9659-15b4f280ee3c.sketch_text.stroke-257"),sQuery(id+"F0.wireOp",EDGE,"46c11c21-c6ca-42b8-9659-15b4f280ee3c.sketch_text.stroke-258"),sQuery(id+"F0.wireOp",EDGE,"46c11c21-c6ca-42b8-9659-15b4f280ee3c.sketch_text.stroke-259"),sQuery(id+"F0.wireOp",EDGE,"46c11c21-c6ca-42b8-9659-15b4f280ee3c.sketch_text.stroke-260")])]});
            var Q6;
            Q6=makeQuery(id+"F1.opExtrude","SWEPT_BODY",BODY,{"disambiguationData":[OSD([sQuery(id+"F0.wireOp",EDGE,"46c11c21-c6ca-42b8-9659-15b4f280ee3c.sketch_text.stroke-230"),sQuery(id+"F0.wireOp",EDGE,"46c11c21-c6ca-42b8-9659-15b4f280ee3c.sketch_text.stroke-231"),sQuery(id+"F0.wireOp",EDGE,"46c11c21-c6ca-42b8-9659-15b4f280ee3c.sketch_text.stroke-232"),sQuery(id+"F0.wireOp",EDGE,"46c11c21-c6ca-42b8-9659-15b4f280ee3c.sketch_text.stroke-233"),sQuery(id+"F0.wireOp",EDGE,"46c11c21-c6ca-42b8-9659-15b4f280ee3c.sketch_text.stroke-234"),sQuery(id+"F0.wireOp",EDGE,"46c11c21-c6ca-42b8-9659-15b4f280ee3c.sketch_text.stroke-235"),sQuery(id+"F0.wireOp",EDGE,"46c11c21-c6ca-42b8-9659-15b4f280ee3c.sketch_text.stroke-236"),sQuery(id+"F0.wireOp",EDGE,"46c11c21-c6ca-42b8-9659-15b4f280ee3c.sketch_text.stroke-237"),sQuery(id+"F0.wireOp",EDGE,"46c11c21-c6ca-42b8-9659-15b4f280ee3c.sketch_text.stroke-238"),sQuery(id+"F0.wireOp",EDGE,"46c11c21-c6ca-42b8-9659-15b4f280ee3c.sketch_text.stroke-239"),sQuery(id+"F0.wireOp",EDGE,"46c11c21-c6ca-42b8-9659-15b4f280ee3c.sketch_text.stroke-240"),sQuery(id+"F0.wireOp",EDGE,"46c11c21-c6ca-42b8-9659-15b4f280ee3c.sketch_text.stroke-241")])]});
            var Q7;
            Q7=makeQuery(id+"F1.opExtrude","SWEPT_BODY",BODY,{"disambiguationData":[OSD([sQuery(id+"F0.wireOp",EDGE,"46c11c21-c6ca-42b8-9659-15b4f280ee3c.sketch_text.stroke-218"),sQuery(id+"F0.wireOp",EDGE,"46c11c21-c6ca-42b8-9659-15b4f280ee3c.sketch_text.stroke-219"),sQuery(id+"F0.wireOp",EDGE,"46c11c21-c6ca-42b8-9659-15b4f280ee3c.sketch_text.stroke-220"),sQuery(id+"F0.wireOp",EDGE,"46c11c21-c6ca-42b8-9659-15b4f280ee3c.sketch_text.stroke-221"),sQuery(id+"F0.wireOp",EDGE,"46c11c21-c6ca-42b8-9659-15b4f280ee3c.sketch_text.stroke-222"),sQuery(id+"F0.wireOp",EDGE,"46c11c21-c6ca-42b8-9659-15b4f280ee3c.sketch_text.stroke-223")])]});
            var Q8;
            Q8=makeQuery(id+"F1.opExtrude","SWEPT_BODY",BODY,{"disambiguationData":[OSD([sQuery(id+"F0.wireOp",EDGE,"46c11c21-c6ca-42b8-9659-15b4f280ee3c.sketch_text.stroke-204"),sQuery(id+"F0.wireOp",EDGE,"46c11c21-c6ca-42b8-9659-15b4f280ee3c.sketch_text.stroke-205"),sQuery(id+"F0.wireOp",EDGE,"46c11c21-c6ca-42b8-9659-15b4f280ee3c.sketch_text.stroke-206"),sQuery(id+"F0.wireOp",EDGE,"46c11c21-c6ca-42b8-9659-15b4f280ee3c.sketch_text.stroke-207"),sQuery(id+"F0.wireOp",EDGE,"46c11c21-c6ca-42b8-9659-15b4f280ee3c.sketch_text.stroke-208"),sQuery(id+"F0.wireOp",EDGE,"46c11c21-c6ca-42b8-9659-15b4f280ee3c.sketch_text.stroke-209"),sQuery(id+"F0.wireOp",EDGE,"46c11c21-c6ca-42b8-9659-15b4f280ee3c.sketch_text.stroke-210"),sQuery(id+"F0.wireOp",EDGE,"46c11c21-c6ca-42b8-9659-15b4f280ee3c.sketch_text.stroke-211"),sQuery(id+"F0.wireOp",EDGE,"46c11c21-c6ca-42b8-9659-15b4f280ee3c.sketch_text.stroke-212"),sQuery(id+"F0.wireOp",EDGE,"46c11c21-c6ca-42b8-9659-15b4f280ee3c.sketch_text.stroke-213"),sQuery(id+"F0.wireOp",EDGE,"46c11c21-c6ca-42b8-9659-15b4f280ee3c.sketch_text.stroke-214"),sQuery(id+"F0.wireOp",EDGE,"46c11c21-c6ca-42b8-9659-15b4f280ee3c.sketch_text.stroke-215"),sQuery(id+"F0.wireOp",EDGE,"46c11c21-c6ca-42b8-9659-15b4f280ee3c.sketch_text.stroke-216"),sQuery(id+"F0.wireOp",EDGE,"46c11c21-c6ca-42b8-9659-15b4f280ee3c.sketch_text.stroke-217")])]});
            var Q9;
            Q9=makeQuery(id+"F1.opExtrude","SWEPT_BODY",BODY,{"disambiguationData":[OSD([sQuery(id+"F0.wireOp",EDGE,"46c11c21-c6ca-42b8-9659-15b4f280ee3c.sketch_text.stroke-29"),sQuery(id+"F0.wireOp",EDGE,"46c11c21-c6ca-42b8-9659-15b4f280ee3c.sketch_text.stroke-30"),sQuery(id+"F0.wireOp",EDGE,"46c11c21-c6ca-42b8-9659-15b4f280ee3c.sketch_text.stroke-31"),sQuery(id+"F0.wireOp",EDGE,"46c11c21-c6ca-42b8-9659-15b4f280ee3c.sketch_text.stroke-32"),sQuery(id+"F0.wireOp",EDGE,"46c11c21-c6ca-42b8-9659-15b4f280ee3c.sketch_text.stroke-33"),sQuery(id+"F0.wireOp",EDGE,"46c11c21-c6ca-42b8-9659-15b4f280ee3c.sketch_text.stroke-34"),sQuery(id+"F0.wireOp",EDGE,"46c11c21-c6ca-42b8-9659-15b4f280ee3c.sketch_text.stroke-35"),sQuery(id+"F0.wireOp",EDGE,"46c11c21-c6ca-42b8-9659-15b4f280ee3c.sketch_text.stroke-36"),sQuery(id+"F0.wireOp",EDGE,"46c11c21-c6ca-42b8-9659-15b4f280ee3c.sketch_text.stroke-37"),sQuery(id+"F0.wireOp",EDGE,"46c11c21-c6ca-42b8-9659-15b4f280ee3c.sketch_text.stroke-38"),sQuery(id+"F0.wireOp",EDGE,"46c11c21-c6ca-42b8-9659-15b4f280ee3c.sketch_text.stroke-39"),sQuery(id+"F0.wireOp",EDGE,"46c11c21-c6ca-42b8-9659-15b4f280ee3c.sketch_text.stroke-40"),sQuery(id+"F0.wireOp",EDGE,"46c11c21-c6ca-42b8-9659-15b4f280ee3c.sketch_text.stroke-41"),sQuery(id+"F0.wireOp",EDGE,"46c11c21-c6ca-42b8-9659-15b4f280ee3c.sketch_text.stroke-42"),sQuery(id+"F0.wireOp",EDGE,"46c11c21-c6ca-42b8-9659-15b4f280ee3c.sketch_text.stroke-43"),sQuery(id+"F0.wireOp",EDGE,"46c11c21-c6ca-42b8-9659-15b4f280ee3c.sketch_text.stroke-44"),sQuery(id+"F0.wireOp",EDGE,"46c11c21-c6ca-42b8-9659-15b4f280ee3c.sketch_text.stroke-45"),sQuery(id+"F0.wireOp",EDGE,"46c11c21-c6ca-42b8-9659-15b4f280ee3c.sketch_text.stroke-46"),sQuery(id+"F0.wireOp",EDGE,"46c11c21-c6ca-42b8-9659-15b4f280ee3c.sketch_text.stroke-47")])]});
            var Q10;
            Q10=makeQuery(id+"F1.opExtrude","SWEPT_BODY",BODY,{"disambiguationData":[OSD([sQuery(id+"F0.wireOp",EDGE,"46c11c21-c6ca-42b8-9659-15b4f280ee3c.sketch_text.stroke-15"),sQuery(id+"F0.wireOp",EDGE,"46c11c21-c6ca-42b8-9659-15b4f280ee3c.sketch_text.stroke-16"),sQuery(id+"F0.wireOp",EDGE,"46c11c21-c6ca-42b8-9659-15b4f280ee3c.sketch_text.stroke-17"),sQuery(id+"F0.wireOp",EDGE,"46c11c21-c6ca-42b8-9659-15b4f280ee3c.sketch_text.stroke-18"),sQuery(id+"F0.wireOp",EDGE,"46c11c21-c6ca-42b8-9659-15b4f280ee3c.sketch_text.stroke-19"),sQuery(id+"F0.wireOp",EDGE,"46c11c21-c6ca-42b8-9659-15b4f280ee3c.sketch_text.stroke-20"),sQuery(id+"F0.wireOp",EDGE,"46c11c21-c6ca-42b8-9659-15b4f280ee3c.sketch_text.stroke-21"),sQuery(id+"F0.wireOp",EDGE,"46c11c21-c6ca-42b8-9659-15b4f280ee3c.sketch_text.stroke-22"),sQuery(id+"F0.wireOp",EDGE,"46c11c21-c6ca-42b8-9659-15b4f280ee3c.sketch_text.stroke-23"),sQuery(id+"F0.wireOp",EDGE,"46c11c21-c6ca-42b8-9659-15b4f280ee3c.sketch_text.stroke-24"),sQuery(id+"F0.wireOp",EDGE,"46c11c21-c6ca-42b8-9659-15b4f280ee3c.sketch_text.stroke-25"),sQuery(id+"F0.wireOp",EDGE,"46c11c21-c6ca-42b8-9659-15b4f280ee3c.sketch_text.stroke-26"),sQuery(id+"F0.wireOp",EDGE,"46c11c21-c6ca-42b8-9659-15b4f280ee3c.sketch_text.stroke-27"),sQuery(id+"F0.wireOp",EDGE,"46c11c21-c6ca-42b8-9659-15b4f280ee3c.sketch_text.stroke-28")])]});
            var Q11;
            Q11=makeQuery(id+"F1.opExtrude","SWEPT_BODY",BODY,{"disambiguationData":[OSD([sQuery(id+"F0.wireOp",EDGE,"E3"),sQuery(id+"F0.wireOp",EDGE,"E4"),sQuery(id+"F0.wireOp",EDGE,"E5"),sQuery(id+"F0.wireOp",EDGE,"E6.0"),sQuery(id+"F0.wireOp",EDGE,"E6.1"),sQuery(id+"F0.wireOp",EDGE,"E6.2"),sQuery(id+"F0.wireOp",EDGE,"E9.filletArc"),sQuery(id+"F0.wireOp",EDGE,"E10.filletArc"),sQuery(id+"F0.wireOp",EDGE,"E12.6.MirrorCS"),sQuery(id+"F0.wireOp",EDGE,"E12.7.MirrorCS"),sQuery(id+"F0.wireOp",EDGE,"E12.8.MirrorCS"),sQuery(id+"F0.wireOp",EDGE,"E12.10.MirrorCS"),sQuery(id+"F0.wireOp",EDGE,"E12.12.MirrorCS"),sQuery(id+"F0.wireOp",EDGE,"E12.13.MirrorCS"),sQuery(id+"F0.wireOp",EDGE,"E12.14.MirrorCS"),sQuery(id+"F0.wireOp",EDGE,"E12.15.MirrorCS"),sQuery(id+"F0.wireOp",EDGE,"E29.filletArc"),sQuery(id+"F0.wireOp",EDGE,"E30.filletArc"),sQuery(id+"F0.wireOp",EDGE,"E31.filletArc"),sQuery(id+"F0.wireOp",EDGE,"E32.filletArc"),sQuery(id+"F0.wireOp",EDGE,"E33.filletArc"),sQuery(id+"F0.wireOp",EDGE,"E34.filletArc"),sQuery(id+"F0.wireOp",EDGE,"E35.filletArc"),sQuery(id+"F0.wireOp",EDGE,"E36.filletArc"),sQuery(id+"F0.wireOp",EDGE,"E37.filletArc"),sQuery(id+"F0.wireOp",EDGE,"E38.filletArc")])]});
            var Q12;
            Q12=makeQuery(id+"F1.opExtrude","SWEPT_BODY",BODY,{"disambiguationData":[OSD([sQuery(id+"F0.wireOp",EDGE,"E12.1.MirrorCS"),sQuery(id+"F0.wireOp",EDGE,"E12.3.MirrorCS"),sQuery(id+"F0.wireOp",EDGE,"E12.4.MirrorCS"),sQuery(id+"F0.wireOp",EDGE,"E12.5.MirrorCS"),sQuery(id+"F0.wireOp",EDGE,"E21.filletArc"),sQuery(id+"F0.wireOp",EDGE,"E22.filletArc"),sQuery(id+"F0.wireOp",EDGE,"E23.filletArc"),sQuery(id+"F0.wireOp",EDGE,"E24.filletArc")])]});
            var Q13;
            Q13=makeQuery(id+"F1.opExtrude","SWEPT_BODY",BODY,{"disambiguationData":[OSD([sQuery(id+"F0.wireOp",EDGE,"E41"),sQuery(id+"F0.wireOp",EDGE,"E42"),sQuery(id+"F0.wireOp",EDGE,"E43"),sQuery(id+"F0.wireOp",EDGE,"E54.trimOffspring")])]});
            var Q14;
            Q14=makeQuery(id+"F1.opExtrude","SWEPT_BODY",BODY,{"disambiguationData":[OSD([sQuery(id+"F0.wireOp",EDGE,"46c11c21-c6ca-42b8-9659-15b4f280ee3c.sketch_text.stroke-163"),sQuery(id+"F0.wireOp",EDGE,"46c11c21-c6ca-42b8-9659-15b4f280ee3c.sketch_text.stroke-164"),sQuery(id+"F0.wireOp",EDGE,"46c11c21-c6ca-42b8-9659-15b4f280ee3c.sketch_text.stroke-165"),sQuery(id+"F0.wireOp",EDGE,"46c11c21-c6ca-42b8-9659-15b4f280ee3c.sketch_text.stroke-166"),sQuery(id+"F0.wireOp",EDGE,"46c11c21-c6ca-42b8-9659-15b4f280ee3c.sketch_text.stroke-167"),sQuery(id+"F0.wireOp",EDGE,"46c11c21-c6ca-42b8-9659-15b4f280ee3c.sketch_text.stroke-168"),sQuery(id+"F0.wireOp",EDGE,"46c11c21-c6ca-42b8-9659-15b4f280ee3c.sketch_text.stroke-169"),sQuery(id+"F0.wireOp",EDGE,"46c11c21-c6ca-42b8-9659-15b4f280ee3c.sketch_text.stroke-170"),sQuery(id+"F0.wireOp",EDGE,"46c11c21-c6ca-42b8-9659-15b4f280ee3c.sketch_text.stroke-171"),sQuery(id+"F0.wireOp",EDGE,"46c11c21-c6ca-42b8-9659-15b4f280ee3c.sketch_text.stroke-172"),sQuery(id+"F0.wireOp",EDGE,"46c11c21-c6ca-42b8-9659-15b4f280ee3c.sketch_text.stroke-173"),sQuery(id+"F0.wireOp",EDGE,"46c11c21-c6ca-42b8-9659-15b4f280ee3c.sketch_text.stroke-174"),sQuery(id+"F0.wireOp",EDGE,"46c11c21-c6ca-42b8-9659-15b4f280ee3c.sketch_text.stroke-175"),sQuery(id+"F0.wireOp",EDGE,"46c11c21-c6ca-42b8-9659-15b4f280ee3c.sketch_text.stroke-176")])]});
            var Q15;
            Q15=makeQuery(id+"F1.opExtrude","SWEPT_BODY",BODY,{"disambiguationData":[OSD([sQuery(id+"F0.wireOp",EDGE,"46c11c21-c6ca-42b8-9659-15b4f280ee3c.sketch_text.stroke-115"),sQuery(id+"F0.wireOp",EDGE,"46c11c21-c6ca-42b8-9659-15b4f280ee3c.sketch_text.stroke-116"),sQuery(id+"F0.wireOp",EDGE,"46c11c21-c6ca-42b8-9659-15b4f280ee3c.sketch_text.stroke-117"),sQuery(id+"F0.wireOp",EDGE,"46c11c21-c6ca-42b8-9659-15b4f280ee3c.sketch_text.stroke-118"),sQuery(id+"F0.wireOp",EDGE,"46c11c21-c6ca-42b8-9659-15b4f280ee3c.sketch_text.stroke-119"),sQuery(id+"F0.wireOp",EDGE,"46c11c21-c6ca-42b8-9659-15b4f280ee3c.sketch_text.stroke-120"),sQuery(id+"F0.wireOp",EDGE,"46c11c21-c6ca-42b8-9659-15b4f280ee3c.sketch_text.stroke-121"),sQuery(id+"F0.wireOp",EDGE,"46c11c21-c6ca-42b8-9659-15b4f280ee3c.sketch_text.stroke-122"),sQuery(id+"F0.wireOp",EDGE,"46c11c21-c6ca-42b8-9659-15b4f280ee3c.sketch_text.stroke-123"),sQuery(id+"F0.wireOp",EDGE,"46c11c21-c6ca-42b8-9659-15b4f280ee3c.sketch_text.stroke-124"),sQuery(id+"F0.wireOp",EDGE,"46c11c21-c6ca-42b8-9659-15b4f280ee3c.sketch_text.stroke-125"),sQuery(id+"F0.wireOp",EDGE,"46c11c21-c6ca-42b8-9659-15b4f280ee3c.sketch_text.stroke-126"),sQuery(id+"F0.wireOp",EDGE,"46c11c21-c6ca-42b8-9659-15b4f280ee3c.sketch_text.stroke-127"),sQuery(id+"F0.wireOp",EDGE,"46c11c21-c6ca-42b8-9659-15b4f280ee3c.sketch_text.stroke-128"),sQuery(id+"F0.wireOp",EDGE,"46c11c21-c6ca-42b8-9659-15b4f280ee3c.sketch_text.stroke-129"),sQuery(id+"F0.wireOp",EDGE,"46c11c21-c6ca-42b8-9659-15b4f280ee3c.sketch_text.stroke-130"),sQuery(id+"F0.wireOp",EDGE,"46c11c21-c6ca-42b8-9659-15b4f280ee3c.sketch_text.stroke-131"),sQuery(id+"F0.wireOp",EDGE,"46c11c21-c6ca-42b8-9659-15b4f280ee3c.sketch_text.stroke-132"),sQuery(id+"F0.wireOp",EDGE,"46c11c21-c6ca-42b8-9659-15b4f280ee3c.sketch_text.stroke-133")])]});
            var Q16;
            Q16=makeQuery(id+"F1.opExtrude","SWEPT_BODY",BODY,{"disambiguationData":[OSD([sQuery(id+"F0.wireOp",EDGE,"46c11c21-c6ca-42b8-9659-15b4f280ee3c.sketch_text.stroke-185"),sQuery(id+"F0.wireOp",EDGE,"46c11c21-c6ca-42b8-9659-15b4f280ee3c.sketch_text.stroke-186"),sQuery(id+"F0.wireOp",EDGE,"46c11c21-c6ca-42b8-9659-15b4f280ee3c.sketch_text.stroke-187"),sQuery(id+"F0.wireOp",EDGE,"46c11c21-c6ca-42b8-9659-15b4f280ee3c.sketch_text.stroke-188"),sQuery(id+"F0.wireOp",EDGE,"46c11c21-c6ca-42b8-9659-15b4f280ee3c.sketch_text.stroke-189"),sQuery(id+"F0.wireOp",EDGE,"46c11c21-c6ca-42b8-9659-15b4f280ee3c.sketch_text.stroke-190"),sQuery(id+"F0.wireOp",EDGE,"46c11c21-c6ca-42b8-9659-15b4f280ee3c.sketch_text.stroke-191"),sQuery(id+"F0.wireOp",EDGE,"46c11c21-c6ca-42b8-9659-15b4f280ee3c.sketch_text.stroke-192"),sQuery(id+"F0.wireOp",EDGE,"46c11c21-c6ca-42b8-9659-15b4f280ee3c.sketch_text.stroke-193"),sQuery(id+"F0.wireOp",EDGE,"46c11c21-c6ca-42b8-9659-15b4f280ee3c.sketch_text.stroke-194"),sQuery(id+"F0.wireOp",EDGE,"46c11c21-c6ca-42b8-9659-15b4f280ee3c.sketch_text.stroke-195"),sQuery(id+"F0.wireOp",EDGE,"46c11c21-c6ca-42b8-9659-15b4f280ee3c.sketch_text.stroke-196"),sQuery(id+"F0.wireOp",EDGE,"46c11c21-c6ca-42b8-9659-15b4f280ee3c.sketch_text.stroke-197"),sQuery(id+"F0.wireOp",EDGE,"46c11c21-c6ca-42b8-9659-15b4f280ee3c.sketch_text.stroke-198"),sQuery(id+"F0.wireOp",EDGE,"46c11c21-c6ca-42b8-9659-15b4f280ee3c.sketch_text.stroke-199"),sQuery(id+"F0.wireOp",EDGE,"46c11c21-c6ca-42b8-9659-15b4f280ee3c.sketch_text.stroke-200"),sQuery(id+"F0.wireOp",EDGE,"46c11c21-c6ca-42b8-9659-15b4f280ee3c.sketch_text.stroke-201"),sQuery(id+"F0.wireOp",EDGE,"46c11c21-c6ca-42b8-9659-15b4f280ee3c.sketch_text.stroke-202"),sQuery(id+"F0.wireOp",EDGE,"46c11c21-c6ca-42b8-9659-15b4f280ee3c.sketch_text.stroke-203")])]});
            var Q17;
            Q17=makeQuery(id+"F1.opExtrude","SWEPT_BODY",BODY,{"disambiguationData":[OSD([sQuery(id+"F0.wireOp",EDGE,"E46.trimOffspring"),sQuery(id+"F0.wireOp",EDGE,"E48.trimOffspring"),sQuery(id+"F0.wireOp",EDGE,"E51.trimOffspring"),sQuery(id+"F0.wireOp",EDGE,"E53.trimOffspring")])]});
            var Q18;
            Q18=makeQuery(id+"F1.opExtrude","SWEPT_BODY",BODY,{"disambiguationData":[OSD([sQuery(id+"F0.wireOp",EDGE,"E11.right"),sQuery(id+"F0.wireOp",EDGE,"E11.left"),sQuery(id+"F0.wireOp",EDGE,"E11.top"),sQuery(id+"F0.wireOp",EDGE,"E11.bottom"),sQuery(id+"F0.wireOp",EDGE,"E25.filletArc"),sQuery(id+"F0.wireOp",EDGE,"E26.filletArc"),sQuery(id+"F0.wireOp",EDGE,"E27.filletArc"),sQuery(id+"F0.wireOp",EDGE,"E28.filletArc")])]});
            var Q19;
            Q19=makeQuery(id+"F1.opExtrude","SWEPT_BODY",BODY,{"disambiguationData":[OSD([sQuery(id+"F0.wireOp",EDGE,"46c11c21-c6ca-42b8-9659-15b4f280ee3c.sketch_text.stroke-224"),sQuery(id+"F0.wireOp",EDGE,"46c11c21-c6ca-42b8-9659-15b4f280ee3c.sketch_text.stroke-225"),sQuery(id+"F0.wireOp",EDGE,"46c11c21-c6ca-42b8-9659-15b4f280ee3c.sketch_text.stroke-226"),sQuery(id+"F0.wireOp",EDGE,"46c11c21-c6ca-42b8-9659-15b4f280ee3c.sketch_text.stroke-227"),sQuery(id+"F0.wireOp",EDGE,"46c11c21-c6ca-42b8-9659-15b4f280ee3c.sketch_text.stroke-228"),sQuery(id+"F0.wireOp",EDGE,"46c11c21-c6ca-42b8-9659-15b4f280ee3c.sketch_text.stroke-229")])]});
            var Q20;
            Q20=makeQuery(id+"F1.opExtrude","SWEPT_BODY",BODY,{"disambiguationData":[OSD([sQuery(id+"F0.wireOp",EDGE,"46c11c21-c6ca-42b8-9659-15b4f280ee3c.sketch_text.stroke-60"),sQuery(id+"F0.wireOp",EDGE,"46c11c21-c6ca-42b8-9659-15b4f280ee3c.sketch_text.stroke-61"),sQuery(id+"F0.wireOp",EDGE,"46c11c21-c6ca-42b8-9659-15b4f280ee3c.sketch_text.stroke-62"),sQuery(id+"F0.wireOp",EDGE,"46c11c21-c6ca-42b8-9659-15b4f280ee3c.sketch_text.stroke-63"),sQuery(id+"F0.wireOp",EDGE,"46c11c21-c6ca-42b8-9659-15b4f280ee3c.sketch_text.stroke-64"),sQuery(id+"F0.wireOp",EDGE,"46c11c21-c6ca-42b8-9659-15b4f280ee3c.sketch_text.stroke-65"),sQuery(id+"F0.wireOp",EDGE,"46c11c21-c6ca-42b8-9659-15b4f280ee3c.sketch_text.stroke-66"),sQuery(id+"F0.wireOp",EDGE,"46c11c21-c6ca-42b8-9659-15b4f280ee3c.sketch_text.stroke-67"),sQuery(id+"F0.wireOp",EDGE,"46c11c21-c6ca-42b8-9659-15b4f280ee3c.sketch_text.stroke-68"),sQuery(id+"F0.wireOp",EDGE,"46c11c21-c6ca-42b8-9659-15b4f280ee3c.sketch_text.stroke-69"),sQuery(id+"F0.wireOp",EDGE,"46c11c21-c6ca-42b8-9659-15b4f280ee3c.sketch_text.stroke-70"),sQuery(id+"F0.wireOp",EDGE,"46c11c21-c6ca-42b8-9659-15b4f280ee3c.sketch_text.stroke-71"),sQuery(id+"F0.wireOp",EDGE,"46c11c21-c6ca-42b8-9659-15b4f280ee3c.sketch_text.stroke-72"),sQuery(id+"F0.wireOp",EDGE,"46c11c21-c6ca-42b8-9659-15b4f280ee3c.sketch_text.stroke-73"),sQuery(id+"F0.wireOp",EDGE,"46c11c21-c6ca-42b8-9659-15b4f280ee3c.sketch_text.stroke-74"),sQuery(id+"F0.wireOp",EDGE,"46c11c21-c6ca-42b8-9659-15b4f280ee3c.sketch_text.stroke-75"),sQuery(id+"F0.wireOp",EDGE,"46c11c21-c6ca-42b8-9659-15b4f280ee3c.sketch_text.stroke-76"),sQuery(id+"F0.wireOp",EDGE,"46c11c21-c6ca-42b8-9659-15b4f280ee3c.sketch_text.stroke-77"),sQuery(id+"F0.wireOp",EDGE,"46c11c21-c6ca-42b8-9659-15b4f280ee3c.sketch_text.stroke-78")])]});
            var Q21;
            Q21=makeQuery(id+"F1.opExtrude","SWEPT_BODY",BODY,{"disambiguationData":[OSD([sQuery(id+"F0.wireOp",EDGE,"E39"),sQuery(id+"F0.wireOp",EDGE,"E40"),sQuery(id+"F0.wireOp",EDGE,"E44.trimOffspring"),sQuery(id+"F0.wireOp",EDGE,"E52.trimOffspring")])]});
            var Q22;
            Q22=makeQuery(id+"F1.opExtrude","SWEPT_BODY",BODY,{"disambiguationData":[OSD([sQuery(id+"F0.wireOp",EDGE,"46c11c21-c6ca-42b8-9659-15b4f280ee3c.sketch_text.stroke-177"),sQuery(id+"F0.wireOp",EDGE,"46c11c21-c6ca-42b8-9659-15b4f280ee3c.sketch_text.stroke-178"),sQuery(id+"F0.wireOp",EDGE,"46c11c21-c6ca-42b8-9659-15b4f280ee3c.sketch_text.stroke-179"),sQuery(id+"F0.wireOp",EDGE,"46c11c21-c6ca-42b8-9659-15b4f280ee3c.sketch_text.stroke-180"),sQuery(id+"F0.wireOp",EDGE,"46c11c21-c6ca-42b8-9659-15b4f280ee3c.sketch_text.stroke-181"),sQuery(id+"F0.wireOp",EDGE,"46c11c21-c6ca-42b8-9659-15b4f280ee3c.sketch_text.stroke-182"),sQuery(id+"F0.wireOp",EDGE,"46c11c21-c6ca-42b8-9659-15b4f280ee3c.sketch_text.stroke-183"),sQuery(id+"F0.wireOp",EDGE,"46c11c21-c6ca-42b8-9659-15b4f280ee3c.sketch_text.stroke-184")])]});
            var Q23;
            Q23=makeQuery(id+"F1.opExtrude","SWEPT_BODY",BODY,{"disambiguationData":[OSD([sQuery(id+"F0.wireOp",EDGE,"46c11c21-c6ca-42b8-9659-15b4f280ee3c.sketch_text.stroke-0"),sQuery(id+"F0.wireOp",EDGE,"46c11c21-c6ca-42b8-9659-15b4f280ee3c.sketch_text.stroke-1"),sQuery(id+"F0.wireOp",EDGE,"46c11c21-c6ca-42b8-9659-15b4f280ee3c.sketch_text.stroke-2"),sQuery(id+"F0.wireOp",EDGE,"46c11c21-c6ca-42b8-9659-15b4f280ee3c.sketch_text.stroke-3"),sQuery(id+"F0.wireOp",EDGE,"46c11c21-c6ca-42b8-9659-15b4f280ee3c.sketch_text.stroke-4"),sQuery(id+"F0.wireOp",EDGE,"46c11c21-c6ca-42b8-9659-15b4f280ee3c.sketch_text.stroke-5"),sQuery(id+"F0.wireOp",EDGE,"46c11c21-c6ca-42b8-9659-15b4f280ee3c.sketch_text.stroke-6"),sQuery(id+"F0.wireOp",EDGE,"46c11c21-c6ca-42b8-9659-15b4f280ee3c.sketch_text.stroke-7"),sQuery(id+"F0.wireOp",EDGE,"46c11c21-c6ca-42b8-9659-15b4f280ee3c.sketch_text.stroke-8"),sQuery(id+"F0.wireOp",EDGE,"46c11c21-c6ca-42b8-9659-15b4f280ee3c.sketch_text.stroke-9"),sQuery(id+"F0.wireOp",EDGE,"46c11c21-c6ca-42b8-9659-15b4f280ee3c.sketch_text.stroke-10"),sQuery(id+"F0.wireOp",EDGE,"46c11c21-c6ca-42b8-9659-15b4f280ee3c.sketch_text.stroke-11"),sQuery(id+"F0.wireOp",EDGE,"46c11c21-c6ca-42b8-9659-15b4f280ee3c.sketch_text.stroke-12"),sQuery(id+"F0.wireOp",EDGE,"46c11c21-c6ca-42b8-9659-15b4f280ee3c.sketch_text.stroke-13"),sQuery(id+"F0.wireOp",EDGE,"46c11c21-c6ca-42b8-9659-15b4f280ee3c.sketch_text.stroke-14")])]});
            var Q24;
            Q24=makeQuery(id+"F1.opExtrude","SWEPT_BODY",BODY,{"disambiguationData":[OSD([sQuery(id+"F0.wireOp",EDGE,"46c11c21-c6ca-42b8-9659-15b4f280ee3c.sketch_text.stroke-48"),sQuery(id+"F0.wireOp",EDGE,"46c11c21-c6ca-42b8-9659-15b4f280ee3c.sketch_text.stroke-49"),sQuery(id+"F0.wireOp",EDGE,"46c11c21-c6ca-42b8-9659-15b4f280ee3c.sketch_text.stroke-50"),sQuery(id+"F0.wireOp",EDGE,"46c11c21-c6ca-42b8-9659-15b4f280ee3c.sketch_text.stroke-51"),sQuery(id+"F0.wireOp",EDGE,"46c11c21-c6ca-42b8-9659-15b4f280ee3c.sketch_text.stroke-52"),sQuery(id+"F0.wireOp",EDGE,"46c11c21-c6ca-42b8-9659-15b4f280ee3c.sketch_text.stroke-53"),sQuery(id+"F0.wireOp",EDGE,"46c11c21-c6ca-42b8-9659-15b4f280ee3c.sketch_text.stroke-54"),sQuery(id+"F0.wireOp",EDGE,"46c11c21-c6ca-42b8-9659-15b4f280ee3c.sketch_text.stroke-55"),sQuery(id+"F0.wireOp",EDGE,"46c11c21-c6ca-42b8-9659-15b4f280ee3c.sketch_text.stroke-56"),sQuery(id+"F0.wireOp",EDGE,"46c11c21-c6ca-42b8-9659-15b4f280ee3c.sketch_text.stroke-57"),sQuery(id+"F0.wireOp",EDGE,"46c11c21-c6ca-42b8-9659-15b4f280ee3c.sketch_text.stroke-58"),sQuery(id+"F0.wireOp",EDGE,"46c11c21-c6ca-42b8-9659-15b4f280ee3c.sketch_text.stroke-59")])]});
            var Q25;
            Q25=makeQuery(id+"F1.opExtrude","SWEPT_BODY",BODY,{"disambiguationData":[OSD([sQuery(id+"F0.wireOp",EDGE,"46c11c21-c6ca-42b8-9659-15b4f280ee3c.sketch_text.stroke-93"),sQuery(id+"F0.wireOp",EDGE,"46c11c21-c6ca-42b8-9659-15b4f280ee3c.sketch_text.stroke-94"),sQuery(id+"F0.wireOp",EDGE,"46c11c21-c6ca-42b8-9659-15b4f280ee3c.sketch_text.stroke-95"),sQuery(id+"F0.wireOp",EDGE,"46c11c21-c6ca-42b8-9659-15b4f280ee3c.sketch_text.stroke-96"),sQuery(id+"F0.wireOp",EDGE,"46c11c21-c6ca-42b8-9659-15b4f280ee3c.sketch_text.stroke-97"),sQuery(id+"F0.wireOp",EDGE,"46c11c21-c6ca-42b8-9659-15b4f280ee3c.sketch_text.stroke-98"),sQuery(id+"F0.wireOp",EDGE,"46c11c21-c6ca-42b8-9659-15b4f280ee3c.sketch_text.stroke-99"),sQuery(id+"F0.wireOp",EDGE,"46c11c21-c6ca-42b8-9659-15b4f280ee3c.sketch_text.stroke-100")])]});
            var Q26;
            Q26=makeQuery(id+"F1.opExtrude","SWEPT_BODY",BODY,{"disambiguationData":[OSD([sQuery(id+"F0.wireOp",EDGE,"E1.bottom"),sQuery(id+"F0.wireOp",EDGE,"E1.top"),sQuery(id+"F0.wireOp",EDGE,"E1.left"),sQuery(id+"F0.wireOp",EDGE,"E1.right"),sQuery(id+"F0.wireOp",EDGE,"E13.filletArc"),sQuery(id+"F0.wireOp",EDGE,"E14.filletArc"),sQuery(id+"F0.wireOp",EDGE,"E15.filletArc"),sQuery(id+"F0.wireOp",EDGE,"E16.filletArc")])]});
            var Q27;
            Q27=makeQuery(id+"F1.opExtrude","SWEPT_BODY",BODY,{"disambiguationData":[OSD([sQuery(id+"F0.wireOp",EDGE,"E45"),sQuery(id+"F0.wireOp",EDGE,"E47"),sQuery(id+"F0.wireOp",EDGE,"E49.trimOffspring"),sQuery(id+"F0.wireOp",EDGE,"E50.trimOffspring")])]});
            var Q28;
            Q28=qCreatedBy(makeId("Origin.pointOp"),VERTEX);
            transform(context, id + "F2", {"entities" : qUnion([Q0, Q1, Q2, Q3, Q4, Q5, Q6, Q7, Q8, Q9, Q10, Q11, Q12, Q13, Q14, Q15, Q16, Q17, Q18, Q19, Q20, Q21, Q22, Q23, Q24, Q25, Q26, Q27]), "transformType" : TransformType.SCALE_UNIFORMLY, "scale" : .357, "makeCopy" : false, "scalePoint" : qUnion([Q28])});
        }
        {
            var Q0;
            Q0=qCreatedBy(makeId("Top.planeOp"),FACE);
            var sketch = newSketch(context, id + "F3", { "sketchPlane" : qUnion([Q0])});
            skText(sketch, "E55", { "text": "C O R E   M O T O R\nC O N T R O L L E R", "fontName": "Arimo-Bold.ttf"});
            const initialGuessF3  = {"E55": [-0.0235, -0.0035, 1, 0, 0.0025]};
            skSetInitialGuess(sketch, initialGuessF3);
            skSolve(sketch);
        }
        {
            var Q0;
            Q0=qSketchRegion(id+"F3",true);
            extrude(context, id + "F4", {"entities" : qUnion([Q0]), "depth" : .1 * mm});
        }
    });
